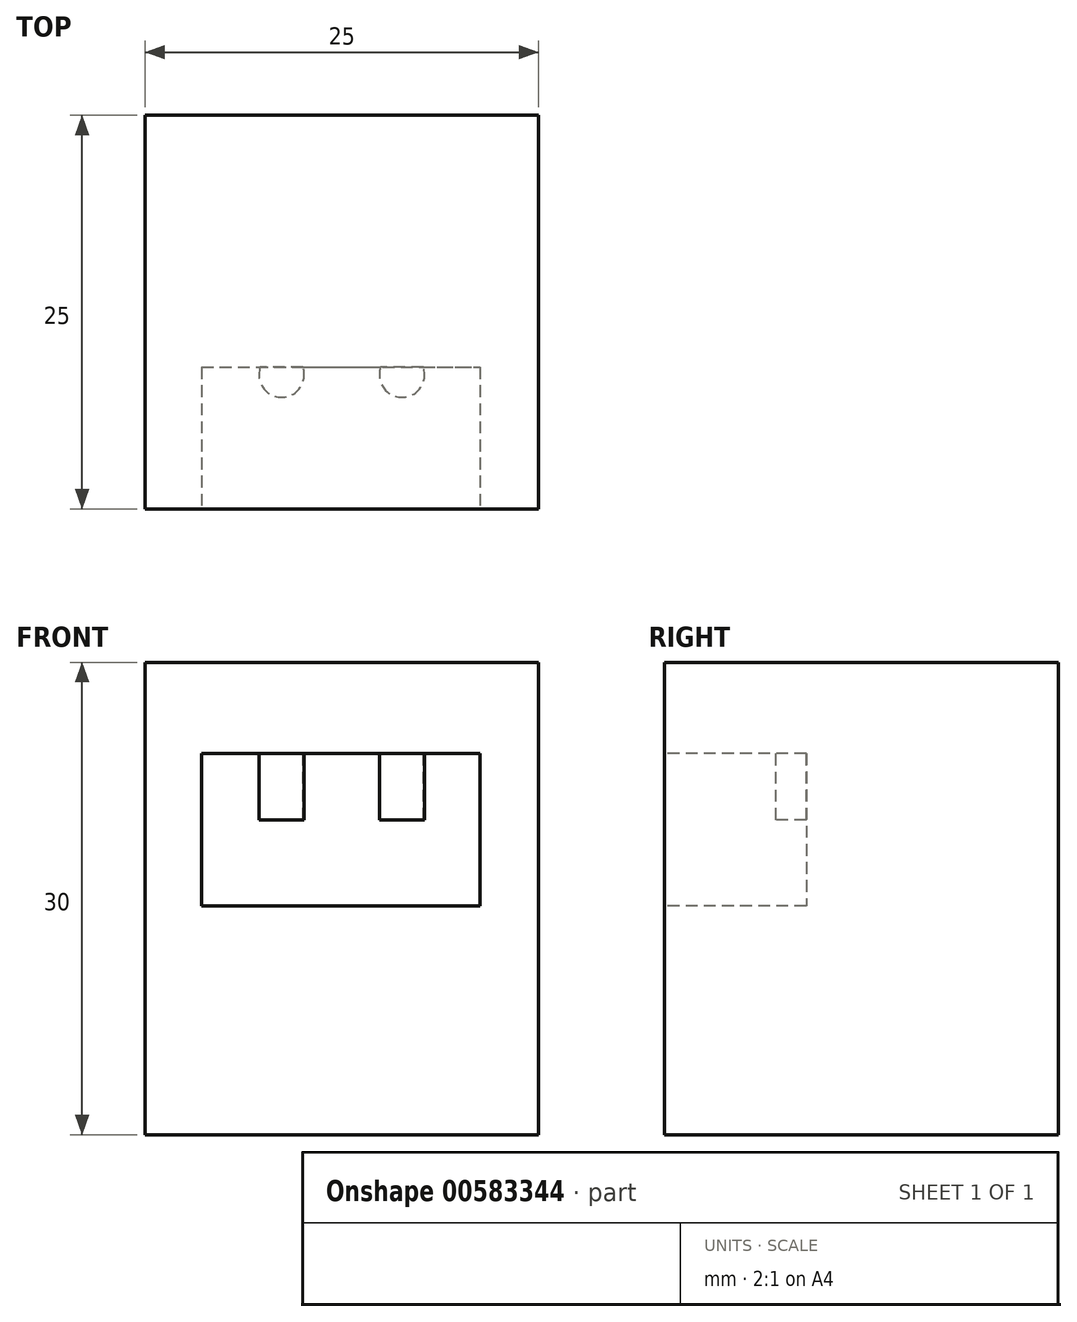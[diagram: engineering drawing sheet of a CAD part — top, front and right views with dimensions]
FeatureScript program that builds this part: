
annotation { "Feature Type Name" : "Feature", "Feature Type Description" : "" }
export const myFeature = defineFeature(function(context is Context, id is Id, definition is map)
    precondition{}
    {
        {
            var Q0;
            Q0=qCreatedBy(makeId("Top.planeOp"),FACE);
            var sketch = newSketch(context, id + "F0", { "sketchPlane" : qUnion([Q0])});
            skLineSegment(sketch, "E0.bottom", {"start": v(-12.5, 12.5) * mm, "end": v(12.5, 12.5) * mm});
            skLineSegment(sketch, "E0.top", {"start": v(-12.5, -12.5) * mm, "end": v(12.5, -12.5) * mm});
            skLineSegment(sketch, "E0.left", {"start": v(-12.5, 12.5) * mm, "end": v(-12.5, -12.5) * mm});
            skLineSegment(sketch, "E0.right", {"start": v(12.5, 12.5) * mm, "end": v(12.5, -12.5) * mm});
            skPoint(sketch, "E0.middle", {"position": v(0, 0) * mm});
            skSolve(sketch);
        }
        {
            var Q0;
            Q0=qCreatedBy(makeId("Top.planeOp"),FACE);
            cPlane(context, id + "F1", {"entities" : qUnion([Q0]), "cplaneType" : CPlaneType.OFFSET, "offset" : 30 * mm, "width" : 150 * mm, "height" : 150 * mm});
        }
        {
            var Q0;
            Q0=makeQuery(id+"F0.imprint","IMPRINT",FACE,{"disambiguationData":[TD([[makeQuery(id+"F0.imprint","IMPRINT",EDGE,{"derivedFrom":sQuery(id+"F0.wireOp",EDGE,"E0.bottom")}),-1.0]])]});
            extrude(context, id + "F2", {"entities" : qUnion([Q0]), "depth" : 30 * mm, "offsetDistance" : 25 * mm});
        }
        {
            var Q0;
            Q0=makeQuery(id+"F2.opExtrude","SWEPT_FACE",FACE,{"disambiguationData":[OSD([sQuery(id+"F0.wireOp",EDGE,"E0.top")])]});
            var sketch = newSketch(context, id + "F3", { "sketchPlane" : qUnion([Q0])});
            skLineSegment(sketch, "E1.bottom", {"start": v(-8.9, 24.22) * mm, "end": v(8.78, 24.22) * mm});
            skLineSegment(sketch, "E1.top", {"start": v(-8.9, 14.53) * mm, "end": v(8.78, 14.53) * mm});
            skLineSegment(sketch, "E1.left", {"start": v(-8.9, 24.22) * mm, "end": v(-8.9, 14.53) * mm});
            skLineSegment(sketch, "E1.right", {"start": v(8.78, 24.22) * mm, "end": v(8.78, 14.53) * mm});
            skCircle(sketch, "E2", {"center": v(0, 48.27) * mm, "radius": 2.51 * mm});
            skArc(sketch, "E3", {"start": v(7.58, 43.9) * mm, "mid": v(8.75, 48.27) * mm, "end": v(7.58, 52.64) * mm});
            skArc(sketch, "E4", {"start": v(2.7, 46.71) * mm, "mid": v(3.11, 48.27) * mm, "end": v(2.7, 49.83) * mm});
            skLineSegment(sketch, "E5", {"start": v(0, 45.16) * mm, "end": v(0, 39.52) * mm});
            skLineSegment(sketch, "E6", {"start": v(0, 51.38) * mm, "end": v(0, 57.02) * mm});
            skLineSegment(sketch, "E7", {"start": v(0, 57.02) * mm, "end": v(0, 51.38) * mm});
            skPoint(sketch, "E8", {"position": v(0, 57.02) * mm});
            skPoint(sketch, "E9", {"position": v(7.58, 43.9) * mm});
            skLineSegment(sketch, "E10", {"start": v(2.7, 49.83) * mm, "end": v(3.79, 50.46) * mm});
            skLineSegment(sketch, "E11", {"start": v(3.79, 50.46) * mm, "end": v(7.58, 52.64) * mm});
            skLineSegment(sketch, "E12", {"start": v(7.58, 52.64) * mm, "end": v(2.7, 49.83) * mm});
            skLineSegment(sketch, "E13.trimOffspring", {"start": v(2.7, 46.71) * mm, "end": v(7.58, 43.9) * mm});
            skLineSegment(sketch, "E14.trimOffspring", {"start": v(-2.7, 49.83) * mm, "end": v(-7.58, 52.64) * mm});
            skLineSegment(sketch, "E15.trimOffspring", {"start": v(-2.7, 46.71) * mm, "end": v(-7.58, 43.9) * mm});
            skArc(sketch, "E16.trimOffspring", {"start": v(0, 57.02) * mm, "mid": v(-4.37, 55.85) * mm, "end": v(-7.58, 52.64) * mm});
            skArc(sketch, "E17.trimOffspring", {"start": v(-2.7, 46.71) * mm, "mid": v(-1.56, 45.57) * mm, "end": v(0, 45.16) * mm});
            skArc(sketch, "E18.trimOffspring", {"start": v(-7.58, 43.9) * mm, "mid": v(-4.37, 40.7) * mm, "end": v(0, 39.52) * mm});
            skArc(sketch, "E19.trimOffspring", {"start": v(0, 51.38) * mm, "mid": v(-1.56, 50.96) * mm, "end": v(-2.7, 49.83) * mm});
            skSolve(sketch);
        }
        {
            var Q0;
            Q0=makeQuery(id+"F3.imprint","IMPRINT",FACE,{"disambiguationData":[TD([[makeQuery(id+"F3.imprint","IMPRINT",EDGE,{"derivedFrom":sQuery(id+"F3.wireOp",EDGE,"E1.bottom")}),-1.0]])]});
            extrude(context, id + "F4", {"entities" : qUnion([Q0]), "operationType" : NewBodyOperationType.REMOVE, "oppositeDirection" : true, "depth" : 9 * mm, "offsetDistance" : 25 * mm});
        }
        {
            var Q0;
            Q0=qCreatedBy(id+"F1.planeOp",FACE);
            var sketch = newSketch(context, id + "F5", { "sketchPlane" : qUnion([Q0])});
            skCircle(sketch, "E20", {"center": v(-3.82, -3.98) * mm, "radius": 1.43 * mm});
            skCircle(sketch, "E21.MirrorC", {"center": v(3.82, -3.98) * mm, "radius": 1.43 * mm});
            skSolve(sketch);
        }
        {
            var Q0;
            Q0=qSketchRegion(id+"F5",true);
            extrude(context, id + "F6", {"entities" : qUnion([Q0]), "operationType" : NewBodyOperationType.ADD, "oppositeDirection" : true, "depth" : 10 * mm, "offsetDistance" : 25 * mm});
        }
    });
